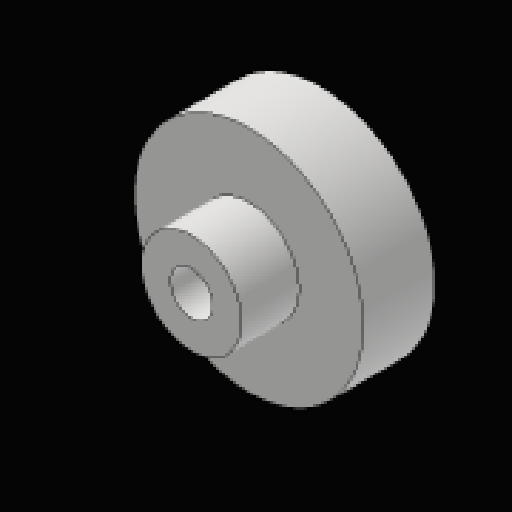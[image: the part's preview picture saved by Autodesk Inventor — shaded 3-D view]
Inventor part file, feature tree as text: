
AUTODESK INVENTOR PART (.ipt)
format: ipt  version: 2023.2 (Build 272271030, 271C)  size: 105,472 bytes
history: native  units: mm
features: extrude x2, sketch x2, projected_geometry x1
ambient origin geometry x8: Origin, YZ Plane, XZ Plane, XY Plane, X Axis, Y Axis, Z Axis, Center Point
bodies: Solid1 (feature_tree)
feature tree (5):
  extrude  "Extrusion1"  Depth=16.0mm
  extrude  "Extrusion2"  Depth=4.0mm
  sketch  "Sketch1"  dims[d0=3.0mm d1=16.0mm]
  sketch  "Sketch2"  dims[d2=5.0mm d3=0.0mm d4=7.0mm d5=4.0mm d6=0.0mm]
  projected_geometry  "Projected Loop1"
